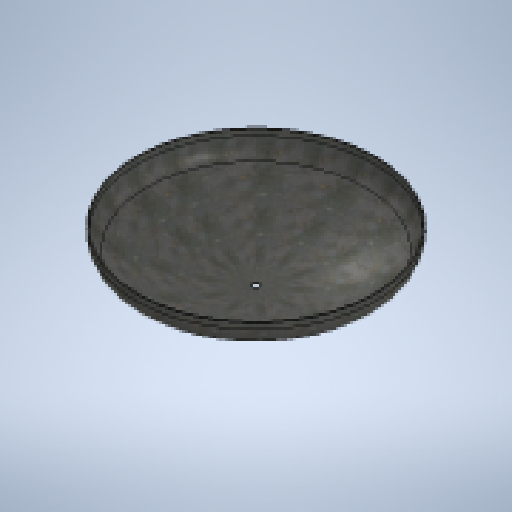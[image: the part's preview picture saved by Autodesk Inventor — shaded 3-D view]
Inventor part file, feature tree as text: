
AUTODESK INVENTOR PART (.ipt)
format: ipt  version: 2025.1 (Build 291241020, 241B)  size: 233,984 bytes
history: native  units: mm
features: sketch x2, revolve x1, extrude x1
ambient origin geometry x8: Origin, YZ Plane, XZ Plane, XY Plane, X Axis, Y Axis, Z Axis, Center Point
bodies: Solid1 (feature_tree)
feature tree (4):
  revolve  "Revolution1"  [1 undecoded]
  extrude  "Extrusion1"  Depth=1084.414286mm
  sketch  "Sketch1"  dims[d0=100.0mm d1=30.0mm]
  sketch  "Sketch2"  dims[d3=1084.414286mm d6=6.0mm d7=90.0deg d8=33.5mm d9=0.0mm d10=0.0mm d11=1200.0mm d12=270.0mm]
note: 1 required parameter value undecoded (feature->parameter linkage not recoverable at this tier; creation-order binding heuristic only, values carry confidence <= 0.55)
